# Revit family: RVT_MACOM_FTC2_AG-AN 12 23 B
name_source: partatom
category: Specialty Equipment
units: mm (PartAtom-declared; Revit-internal decimal feet)

## family parameters
Always vertical = Yes
Cut with Voids When Loaded = No
OmniClass Number = 23.40.40.14.17.24
OmniClass Title = Fryers
Part Type = Normal
Room Calculation Point = No
Round Connector Dimension = Use Diameter
Shared = No
Work Plane-Based = No

## types (2) — shared parameters
Default Elevation = 0,000 mm
Depth = 785,000 mm
Description = FRITADEIRA A GAS MACOM COMERCIAL SPLIT 12,5+12,5 LITROS
Gas Connection Height = 73,000 mm
Gas Size = 3/4"
Height = 1160,000 mm
Manufacturer = MACOM
Oil Capacity = 25,0 L
Show Clearances = Yes
URL = https://www.acosmacom.com.br
Volume = 0,36 m³
Weight = 56,00 kg
Width = 400,000 mm
Work Temperature = 80 °C - 180 °C

## per-type parameters (varying)
| type | Gas Consumption GLP | Gas Consumption GN | Gas Input GLP | Gas Input GN | Gas Pressure |
| FTC2-AG | 1,80 Kg/h | 0 m³/h | 82000 Btu/h |  | 0,03 bar |
| FTC2-AN |  | 2 m³/h | 0 Btu/h | 20665 Kcal/h | 0,02 bar |

note: column(s) folded — value = type name in every type: Model

## geometry (parser evidence)
native form markers: Sweep x10
no freeform markers — native parametric forms only
